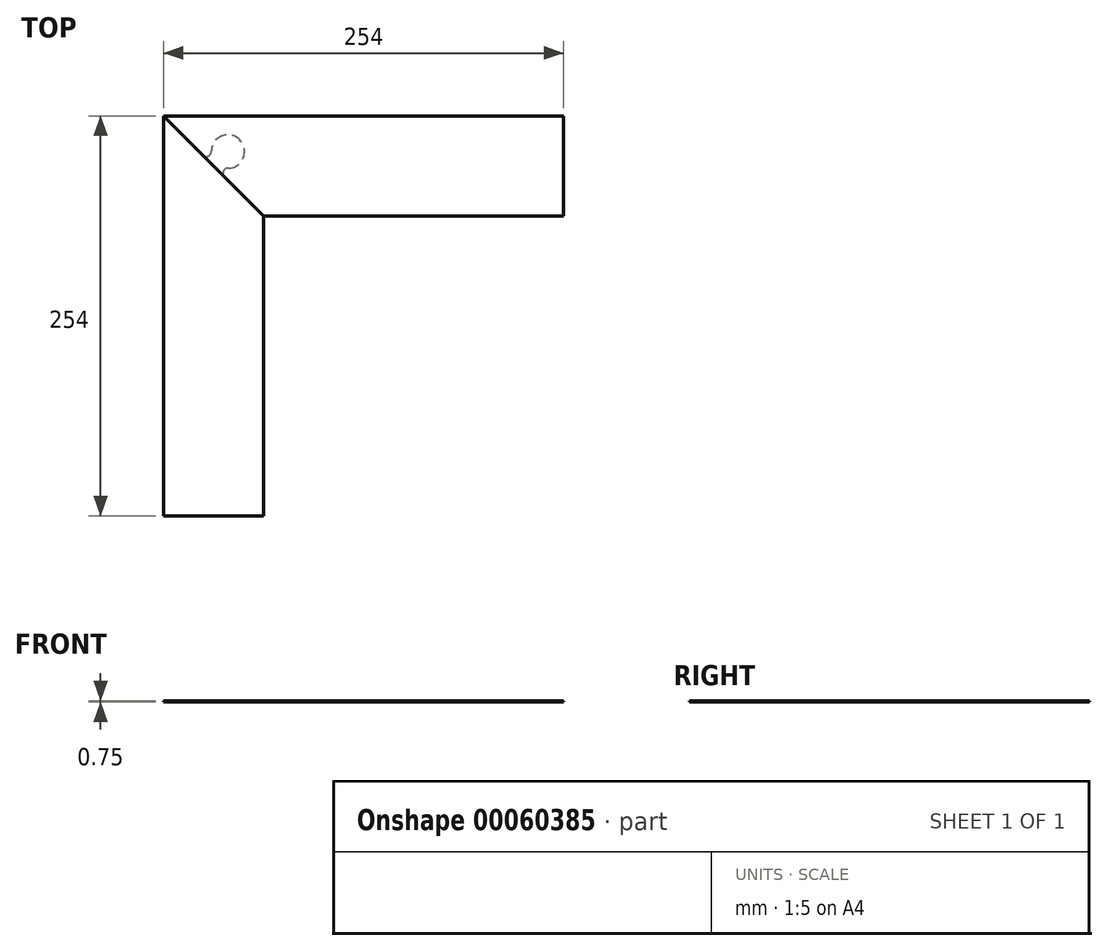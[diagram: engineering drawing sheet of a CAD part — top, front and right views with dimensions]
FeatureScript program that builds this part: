
annotation { "Feature Type Name" : "Feature", "Feature Type Description" : "" }
export const myFeature = defineFeature(function(context is Context, id is Id, definition is map)
    precondition{}
    {
        {
            assignVariable(context, id + "F0", {"name" : "t", "anyValue" : .75});
        }
        {
            var Q0;
            Q0=qCreatedBy(makeId("Top.planeOp"),FACE);
            var sketch = newSketch(context, id + "F1", { "sketchPlane" : qUnion([Q0])});
            skLineSegment(sketch, "E0.bottom", {"start": v(0, 0) * mm, "end": v(63.5, 0) * mm});
            skLineSegment(sketch, "E0.top", {"start": v(0, 254) * mm, "end": v(63.5, 254) * mm});
            skLineSegment(sketch, "E0.left", {"start": v(0, 0) * mm, "end": v(0, 254) * mm});
            skLineSegment(sketch, "E0.right", {"start": v(63.5, 0) * mm, "end": v(63.5, 254) * mm});
            skLineSegment(sketch, "E1", {"start": v(0, 254) * mm, "end": v(63.5, 190.5) * mm});
            skSolve(sketch);
        }
        {
            var Q0;
            {var subQ0=sQuery(id+"F1.wireOp",EDGE,"E0.bottom");Q0=makeQuery(id+"F1.imprint","IMPRINT",FACE,{"disambiguationData":[TD([[makeQuery(id+"F1.imprint","IMPRINT",EDGE,{"derivedFrom":subQ0}),1.0]])]});}
            extrude(context, id + "F2", {"entities" : qUnion([Q0]), "depth" : (getVariable(context, 't')) * mm});
        }
        {
            var Q0;
            Q0=makeQuery(id+"F2.opExtrude","CAP_FACE",FACE,{"disambiguationData":[OSD([sQuery(id+"F1.wireOp",EDGE,"E0.bottom"),sQuery(id+"F1.wireOp",EDGE,"E0.left"),sQuery(id+"F1.wireOp",EDGE,"E0.right"),sQuery(id+"F1.wireOp",EDGE,"E1")])],"isStart":true});
            var sketch = newSketch(context, id + "F3", { "sketchPlane" : qUnion([Q0])});
            skLineSegment(sketch, "E2", {"start": v(0, -254) * mm, "end": v(63.5, -254) * mm, "construction": true});
            skLineSegment(sketch, "E3", {"start": v(63.5, -254) * mm, "end": v(63.5, -190.5) * mm, "construction": true});
            skLineSegment(sketch, "E4", {"start": v(63.5, -254) * mm, "end": v(31.75, -222.25) * mm, "construction": true});
            skCircle(sketch, "E5", {"center": v(40.87, -231.37) * mm, "radius": 10.58 * mm});
            skCircle(sketch, "E6", {"center": v(40.87, -217.62) * mm, "radius": 3.18 * mm});
            skCircle(sketch, "E7", {"center": v(27.12, -231.37) * mm, "radius": 3.18 * mm});
            skLineSegment(sketch, "E8", {"start": v(40.87, -231.37) * mm, "end": v(40.87, -217.62) * mm, "construction": true});
            skSolve(sketch);
        }
        {
            var Q0;
            {var subQ0=sQuery(id+"F3.wireOp",EDGE,"E5");var subQ1=makeQuery(id+"F3.imprint","INTERSECT",VERTEX,{"derivedFrom":[subQ0,sQuery(id+"F3.wireOp",EDGE,"E6")]});Q0=makeQuery(id+"F3.imprint","IMPRINT",FACE,{"disambiguationData":[TD([[makeQuery(id+"F3.imprint","IMPRINT",EDGE,{"disambiguationData":[TD([[subQ1,-1.0]])],"derivedFrom":subQ0}),1.0]])]});}
            var Q1;
            {var subQ0=sQuery(id+"F3.wireOp",EDGE,"E6");var subQ1=sQuery(id+"F3.wireOp",EDGE,"E5");var subQ2=makeQuery(id+"F3.imprint","INTERSECT",VERTEX,{"derivedFrom":[subQ1,subQ0]});Q1=makeQuery(id+"F3.imprint","IMPRINT",FACE,{"disambiguationData":[TD([[makeQuery(id+"F3.imprint","IMPRINT",EDGE,{"disambiguationData":[TD([[subQ2,-1.0]])],"derivedFrom":subQ1}),-1.0]])]});}
            extrude(context, id + "F4", {"entities" : qUnion([Q0, Q1]), "operationType" : NewBodyOperationType.ADD, "oppositeDirection" : true, "depth" : (getVariable(context, 't') / 2) * mm});
        }
        {
            var Q0;
            Q0=qCreatedBy(makeId("Top.planeOp"),FACE);
            var sketch = newSketch(context, id + "F5", { "sketchPlane" : qUnion([Q0])});
            skLineSegment(sketch, "E9.0", {"start": v(0, 254) * mm, "end": v(63.5, 190.5) * mm, "construction": true});
            skLineSegment(sketch, "E10.0", {"start": v(0, 0) * mm, "end": v(0, 254) * mm, "construction": true});
            skLineSegment(sketch, "E11.bottom", {"start": v(0, 254) * mm, "end": v(254, 254) * mm});
            skLineSegment(sketch, "E11.top", {"start": v(0, 190.5) * mm, "end": v(254, 190.5) * mm});
            skLineSegment(sketch, "E11.left", {"start": v(0, 254) * mm, "end": v(0, 190.5) * mm});
            skLineSegment(sketch, "E11.right", {"start": v(254, 254) * mm, "end": v(254, 190.5) * mm});
            skSolve(sketch);
        }
        {
            var Q0;
            Q0 = qSketchRegion(id + "F5", true);
            extrude(context, id + "F6", {"entities" : qUnion([Q0]), "depth" : (getVariable(context, 't')) * mm});
        }
        {
            var Q0;
            Q0=makeQuery(id+"F2.opExtrude","SWEPT_BODY",BODY,{"disambiguationData":[OSD([sQuery(id+"F1.wireOp",EDGE,"E0.bottom"),sQuery(id+"F1.wireOp",EDGE,"E0.left"),sQuery(id+"F1.wireOp",EDGE,"E0.right"),sQuery(id+"F1.wireOp",EDGE,"E1")])]});
            var Q1;
            Q1=makeQuery(id+"F6.opExtrude","SWEPT_BODY",BODY,{"disambiguationData":[OSD([sQuery(id+"F5.wireOp",EDGE,"E11.bottom"),sQuery(id+"F5.wireOp",EDGE,"E11.top"),sQuery(id+"F5.wireOp",EDGE,"E11.left"),sQuery(id+"F5.wireOp",EDGE,"E11.right")])]});
            booleanBodies(context, id + "F7", {"operationType" : BooleanOperationType.SUBTRACTION, "tools" : qUnion([Q0]), "targets" : qUnion([Q1]), "keepTools" : true});
        }
    });
